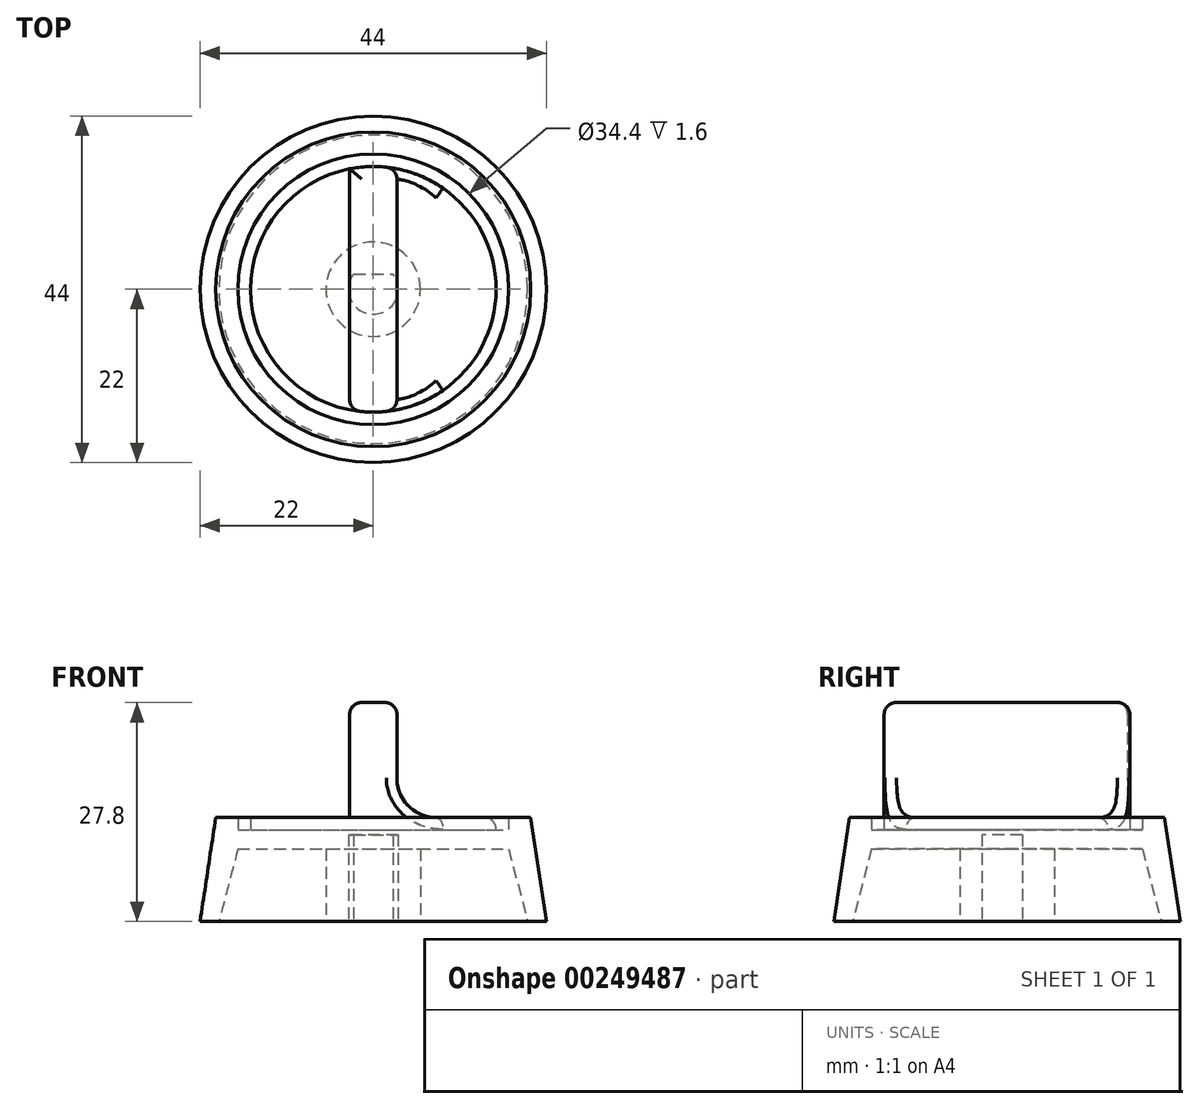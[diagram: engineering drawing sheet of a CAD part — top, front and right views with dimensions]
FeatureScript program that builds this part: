
annotation { "Feature Type Name" : "Feature", "Feature Type Description" : "" }
export const myFeature = defineFeature(function(context is Context, id is Id, definition is map)
    precondition{}
    {
        {
            var Q0;
            Q0=qCreatedBy(makeId("Front.planeOp"),FACE);
            var sketch = newSketch(context, id + "F0", { "sketchPlane" : qUnion([Q0])});
            skLineSegment(sketch, "E0", {"start": v(-22, 0) * mm, "end": v(-20, 13.2) * mm});
            skLineSegment(sketch, "E1", {"start": v(-20, 13.2) * mm, "end": v(-17.2, 13.2) * mm});
            skLineSegment(sketch, "E2", {"start": v(-17.2, 13.2) * mm, "end": v(-17.2, 11.6) * mm});
            skLineSegment(sketch, "E3", {"start": v(-17.2, 11.6) * mm, "end": v(-15.6, 11.6) * mm});
            skLineSegment(sketch, "E4", {"start": v(-15.6, 11.6) * mm, "end": v(-15.6, 13.2) * mm});
            skLineSegment(sketch, "E5", {"start": v(-15.6, 13.2) * mm, "end": v(0, 13.2) * mm});
            skLineSegment(sketch, "E6", {"start": v(0, 13.2) * mm, "end": v(0, 0) * mm});
            skLineSegment(sketch, "E7", {"start": v(0, 0) * mm, "end": v(-6, 0) * mm});
            skLineSegment(sketch, "E8", {"start": v(-6, 0) * mm, "end": v(-6, 9.2) * mm});
            skLineSegment(sketch, "E9", {"start": v(-6, 9.2) * mm, "end": v(-17.2, 9.2) * mm});
            skLineSegment(sketch, "E10", {"start": v(-17.2, 9.2) * mm, "end": v(-19.6, 0) * mm});
            skLineSegment(sketch, "E11", {"start": v(-19.6, 0) * mm, "end": v(-22, 0) * mm});
            skLineSegment(sketch, "E12", {"start": v(0, -10.97) * mm, "end": v(0, 18.45) * mm, "construction": true});
            skSolve(sketch);
        }
        {
            var Q0;
            Q0=makeQuery(id+"F0.imprint","IMPRINT",FACE,{"disambiguationData":[TD([[makeQuery(id+"F0.imprint","IMPRINT",EDGE,{"derivedFrom":sQuery(id+"F0.wireOp",EDGE,"E0")}),-1.0]])]});
            var Q1;
            Q1=sQuery(id+"F0.wireOp",EDGE,"E12");
            revolve(context, id + "F1", {"entities" : qUnion([Q0]), "axis" : qUnion([Q1]), "revolveType" : RevolveType.FULL});
        }
        {
            var Q0;
            Q0=makeQuery(id+"F1.opRevolve","SWEPT_FACE",FACE,{"disambiguationData":[OSD([sQuery(id+"F0.wireOp",EDGE,"E5")])]});
            var sketch = newSketch(context, id + "F2", { "sketchPlane" : qUnion([Q0])});
            skLineSegment(sketch, "E13", {"start": v(-3, 15.3) * mm, "end": v(-3, -15.3) * mm});
            skLineSegment(sketch, "E14", {"start": v(3, 15.3) * mm, "end": v(3, -15.3) * mm});
            skSolve(sketch);
        }
        {
            var Q0;
            {var subQ0=sQuery(id+"F2.wireOp",EDGE,"E13");Q0=makeQuery(id+"F2.imprint","IMPRINT",FACE,{"disambiguationData":[TD([[makeQuery(id+"F2.imprint","IMPRINT",EDGE,{"derivedFrom":subQ0}),1.0]])]});}
            extrude(context, id + "F3", {"entities" : qUnion([Q0]), "operationType" : NewBodyOperationType.ADD, "depth" : 14.6 * mm});
        }
        {
            var Q0;
            Q0=makeQuery(id+"F3.opExtrude","CAP_EDGE",EDGE,{"disambiguationData":[OSD([sQuery(id+"F2.wireOp",EDGE,"E13")])],"isStart":true});
            var Q1;
            Q1=makeQuery(id+"F3.opExtrude","CAP_EDGE",EDGE,{"disambiguationData":[OSD([sQuery(id+"F2.wireOp",EDGE,"E14")])],"isStart":true});
            fillet(context, id + "F4", {"entities" : qUnion([Q0, Q1]), "radius" : 5 * mm, "tangentPropagation" : true, "allowEdgeOverflow" : false});
        }
        {
            var Q0;
            Q0=makeQuery(id+"F3.opExtrude","CAP_EDGE",EDGE,{"disambiguationData":[OSD([sQuery(id+"F2.wireOp",EDGE,"E14")])],"isStart":false});
            var Q1;
            Q1=makeQuery(id+"F3.opExtrude","CAP_EDGE",EDGE,{"disambiguationData":[OSD([sQuery(id+"F2.wireOp",EDGE,"E13")])],"isStart":false});
            var Q2;
            {var subQ0=sQuery(id+"F0.wireOp",EDGE,"E5");var subQ1=sQuery(id+"F0.wireOp",EDGE,"E4");var subQ2=makeQuery(id+"F1.opRevolve","SWEPT_EDGE",EDGE,{"disambiguationData":[OSD([subQ1,subQ0])]});Q2=makeQuery(id+"F3.opExtrude","CAP_EDGE",EDGE,{"disambiguationData":[OSD([subQ1,subQ0]),TDD([makeQuery(id+"F2.imprint","IMPRINT",EDGE,{"disambiguationData":[TD([[makeQuery(id+"F2.imprint","INTERSECT",VERTEX,{"disambiguationData":[OD(1.0)],"derivedFrom":[subQ2,sQuery(id+"F2.wireOp",EDGE,"E13")]}),1.0]])],"derivedFrom":subQ2})])],"isStart":false});}
            var Q3;
            {var subQ0=sQuery(id+"F2.wireOp",EDGE,"E13");var subQ1=sQuery(id+"F0.wireOp",EDGE,"E5");var subQ2=sQuery(id+"F0.wireOp",EDGE,"E4");Q3=makeQuery(id+"F3.opExtrude","SWEPT_EDGE",EDGE,{"disambiguationData":[OSD([subQ2,subQ1,subQ0]),TDD([makeQuery(id+"F2.imprint","INTERSECT",VERTEX,{"disambiguationData":[OD(1.0)],"derivedFrom":[makeQuery(id+"F1.opRevolve","SWEPT_EDGE",EDGE,{"disambiguationData":[OSD([subQ2,subQ1])]}),subQ0]})])]});}
            var Q4;
            {var subQ0=sQuery(id+"F2.wireOp",EDGE,"E14");var subQ1=sQuery(id+"F0.wireOp",EDGE,"E5");var subQ2=sQuery(id+"F0.wireOp",EDGE,"E4");Q4=makeQuery(id+"F3.opExtrude","SWEPT_EDGE",EDGE,{"disambiguationData":[OSD([subQ2,subQ1,subQ0]),TDD([makeQuery(id+"F2.imprint","INTERSECT",VERTEX,{"disambiguationData":[OD(1.0)],"derivedFrom":[makeQuery(id+"F1.opRevolve","SWEPT_EDGE",EDGE,{"disambiguationData":[OSD([subQ2,subQ1])]}),subQ0]})])]});}
            var Q5;
            {var subQ0=sQuery(id+"F0.wireOp",EDGE,"E5");var subQ1=sQuery(id+"F0.wireOp",EDGE,"E4");var subQ2=makeQuery(id+"F1.opRevolve","SWEPT_EDGE",EDGE,{"disambiguationData":[OSD([subQ1,subQ0])]});Q5=makeQuery(id+"F3.opExtrude","CAP_EDGE",EDGE,{"disambiguationData":[OSD([subQ1,subQ0]),TDD([makeQuery(id+"F2.imprint","IMPRINT",EDGE,{"disambiguationData":[TD([[makeQuery(id+"F2.imprint","INTERSECT",VERTEX,{"disambiguationData":[OD(0.0)],"derivedFrom":[subQ2,sQuery(id+"F2.wireOp",EDGE,"E13")]}),-1.0]])],"derivedFrom":subQ2})])],"isStart":false});}
            fillet(context, id + "F5", {"entities" : qUnion([Q0, Q1, Q2, Q3, Q4, Q5]), "radius" : 1.5 * mm, "tangentPropagation" : true, "allowEdgeOverflow" : false});
        }
        {
            var Q0;
            Q0=makeQuery(id+"F1.opRevolve","SWEPT_FACE",FACE,{"disambiguationData":[OSD([sQuery(id+"F0.wireOp",EDGE,"E7")])]});
            var sketch = newSketch(context, id + "F6", { "sketchPlane" : qUnion([Q0])});
            skCircle(sketch, "E15", {"center": v(0, 0) * mm, "radius": 3.17 * mm});
            skLineSegment(sketch, "E16", {"start": v(-2.5, -1.94) * mm, "end": v(2.5, -1.94) * mm});
            skSolve(sketch);
        }
        {
            var Q0;
            {var subQ0=sQuery(id+"F6.wireOp",EDGE,"E16");Q0=makeQuery(id+"F6.imprint","IMPRINT",FACE,{"disambiguationData":[TD([[makeQuery(id+"F6.imprint","IMPRINT",EDGE,{"derivedFrom":subQ0}),1.0]])]});}
            extrude(context, id + "F7", {"entities" : qUnion([Q0]), "operationType" : NewBodyOperationType.REMOVE, "oppositeDirection" : true, "depth" : 11 * mm});
        }
    });
